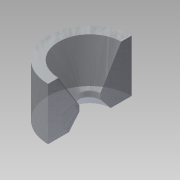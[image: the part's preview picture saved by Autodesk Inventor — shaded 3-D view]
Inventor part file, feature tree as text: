
AUTODESK INVENTOR PART (.ipt)
format: ipt  version: 2014 (Build 180170000, 170)  size: 130,048 bytes
history: native  units: mm
features: other x3, revolve x1, fillet x1, sketch x1
ambient origin geometry x8: Origin, YZ Plane, XZ Plane, XY Plane, X Axis, Y Axis, Z Axis, Center Point
bodies: Body1 (feature_tree)
feature tree (6):
  other  "CrossSection1"
  other  "CrossSection2"
  other  "CrossSection3"
  revolve  "Revolution2"  Angle=90.0deg
  fillet  "Fillet3"  Radius=1.0mm
  sketch  "Sketch2"  dims[d4=5.0mm d13=90.0deg d16=1.0mm d17=0.2mm d18=2.0mm d20=0.5mm d21=2.0mm d22=0.0mm d23=20.0mm d24=1.0mm d25=4.0mm d26=0.5mm d27=2.0mm d28=0.0mm d29=20.0mm d30=0.5mm d31=2.0mm d32=0.0mm d33=20.0mm]
